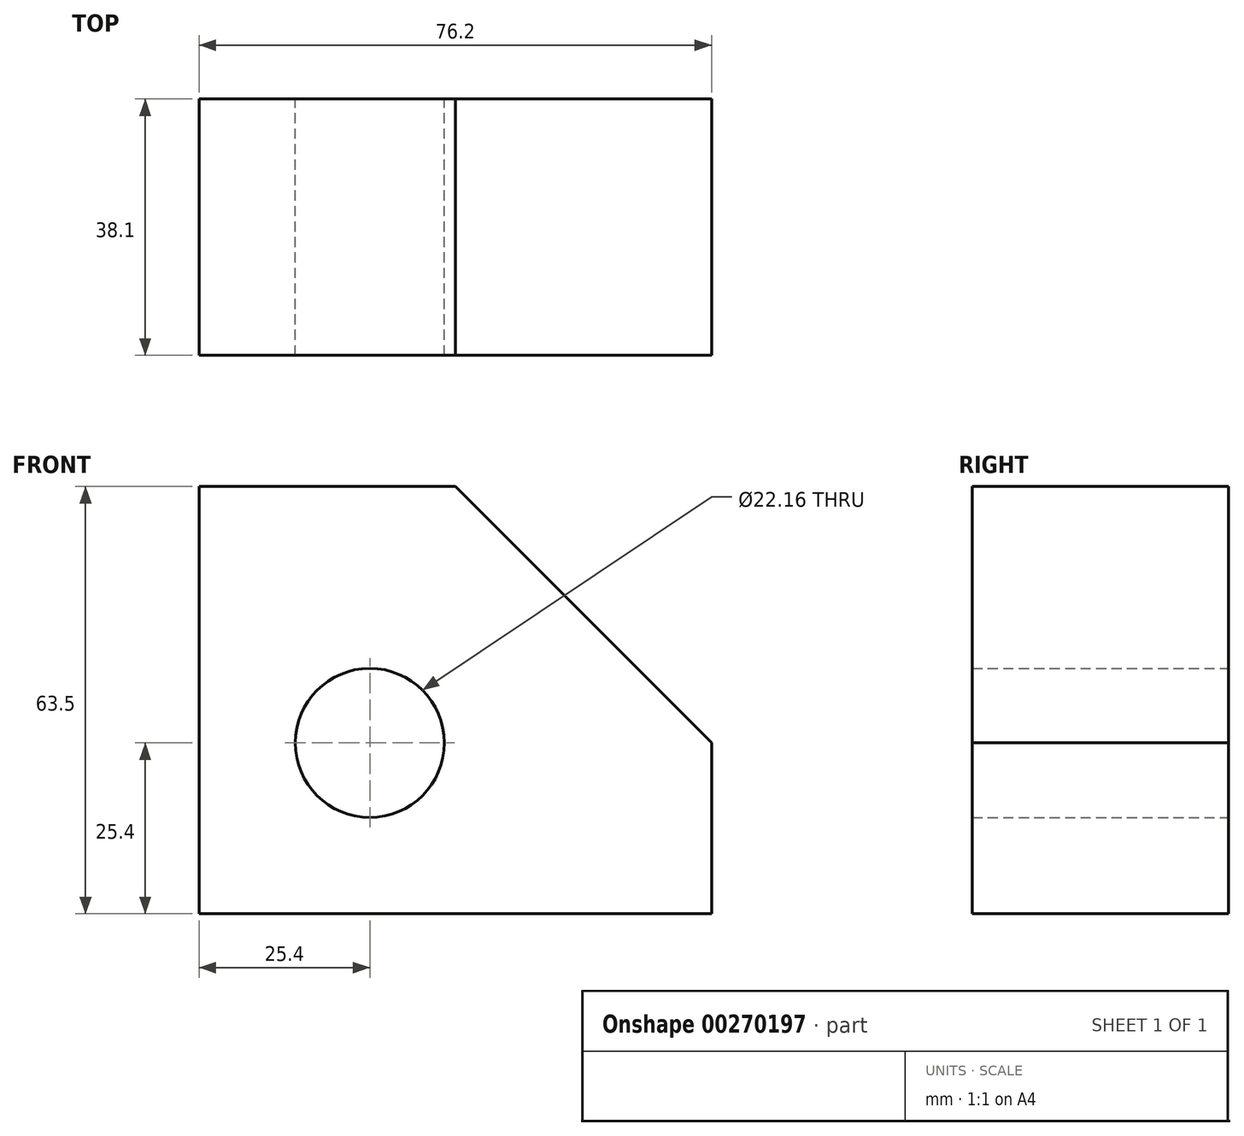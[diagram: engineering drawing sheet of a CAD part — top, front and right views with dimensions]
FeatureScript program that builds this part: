
annotation { "Feature Type Name" : "Feature", "Feature Type Description" : "" }
export const myFeature = defineFeature(function(context is Context, id is Id, definition is map)
    precondition{}
    {
        {
            var Q0;
            Q0=qCreatedBy(makeId("Front.planeOp"),FACE);
            var sketch = newSketch(context, id + "F0", { "sketchPlane" : qUnion([Q0])});
            skLineSegment(sketch, "E0", {"start": v(0, 0) * mm, "end": v(76.2, 0) * mm});
            skLineSegment(sketch, "E1", {"start": v(76.2, 0) * mm, "end": v(76.2, 25.4) * mm});
            skLineSegment(sketch, "E2", {"start": v(76.2, 25.4) * mm, "end": v(38.1, 63.5) * mm});
            skLineSegment(sketch, "E3", {"start": v(38.1, 63.5) * mm, "end": v(0, 63.5) * mm});
            skLineSegment(sketch, "E4", {"start": v(0, 63.5) * mm, "end": v(0, 0) * mm});
            skCircle(sketch, "E5", {"center": v(25.4, 25.4) * mm, "radius": 11.08 * mm});
            skSolve(sketch);
        }
        {
            var Q0;
            Q0=makeQuery(id+"F0.imprint","IMPRINT",FACE,{"disambiguationData":[TD([[makeQuery(id+"F0.imprint","IMPRINT",EDGE,{"derivedFrom":sQuery(id+"F0.wireOp",EDGE,"E0")}),1.0]])]});
            extrude(context, id + "F1", {"entities" : qUnion([Q0]), "depth" : 38.1 * mm, "symmetric" : true});
        }
    });
